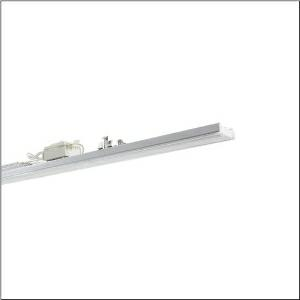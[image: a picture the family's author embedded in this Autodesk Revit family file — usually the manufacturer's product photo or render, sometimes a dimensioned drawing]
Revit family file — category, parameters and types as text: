
# Revit family: licross_r__21_recessed_mo_52tl18cn49xg_ed6d
name_source: partatom
category: Lighting Fixtures
units: mm (PartAtom-declared; Revit-internal decimal feet)

## family parameters
Cut with Voids When Loaded = No
Host = Face
Light Source = No
Part Type = Normal
Room Calculation Point = No
Round Connector Dimension = Use Diameter
Shared = No

## types (1)
- --- (1 x LED, 9000 lm, 49.9 W, 4000K)
    Apparent Load = 50 VA
    CIE Flux Codes = 79 95 99 100 100
    Color Rendering = 80
    Color Temperature = 4000K
    Default Elevation = 1800 mm
    Description = Licross® 21 Recessed MO, luminaire insert, of sheet steel, galvanised, coil coated, white, length: 1.500mm, width: 66mm, height: 67mm, LED rated luminous flux: 9.000lm, light colour: 840, control gear: ON/OFF Multilumen, CLOi, control gear: ECG Multilumen, with plug, 3-pole, with phase selection, mains connection: 220..240V, AC, 50/60Hz, internal wiring halogen-free, primary light control with lens, of plastic, primary optical cover: cover, of PMMA, light emission: direct distribution, primary light characteristic: symmetric, protection rating (complete): IP40, insulation class (complete): insulation class I (protective earthing), certification: CE, ENEC, VDE, UKCA, protection symbol: D if used in an environment without relevant dust loads with corresponding accessories, impact resistance: IK06, permissible ambient temperature for indoor applications: -35..+40°C, corresponds to IFS (International Featured Standards) requirements for safety and quality in the food industry, reducing of maximum allowable ambient temperature of 5°C with ceiling mounting, LABS conformity tested according to VDMA 24364:2018-05, packaging unit: 1 piece
    Height = 58 mm
    Lamp = 1 x LED
    Lamp Light Flux = 9000 lm
    Lamp Power = 49.9 W
    Lamp count = 1
    Length = 1500 mm
    Luminous efficacy = 180 lm/W
    Manufacturer = Siteco
    ModVariant = No
    Model = 52TL18CN49XG
    Mounting Place = Ceiling
    Mounting Type = Pendant
    Number of Poles = 1
    OnlyDefault = Yes
    Power Factor = 1
    Product Name = Licross® 21 Recessed MO
    Product group = luminaire insert | ceiling pendant
    ProductGroupID = 902
    Protection Class = Protection class I
    Protection Degree = IP 40
    RLX_Detail_Level = 1
    RLX_Emergency_Light_Flux = 0 lm
    RLX_Emergency_Type = 0
    RLX_Emergency_Type_DB = No
    RlxData = <blob elided: 22321 chars, md5=c7133551>
    Socket = socket
    Standby Power = 0 W
    System Light Flux = 9000 lm
    System Power = 50 W
    Type Comments = factory setting: luminous flux: 100 % | (A | C | E) | 116 mA
    Type Image = l_1296930.jpg
    URL = http://relux.com
    VarID = @adj_131511
    Voltage = 0 V
    Weight = 0.00 kg
    Width = 66 mm

## geometry (parser evidence)
native form markers: Blend x4, Sweep x10
no freeform markers — native parametric forms only
